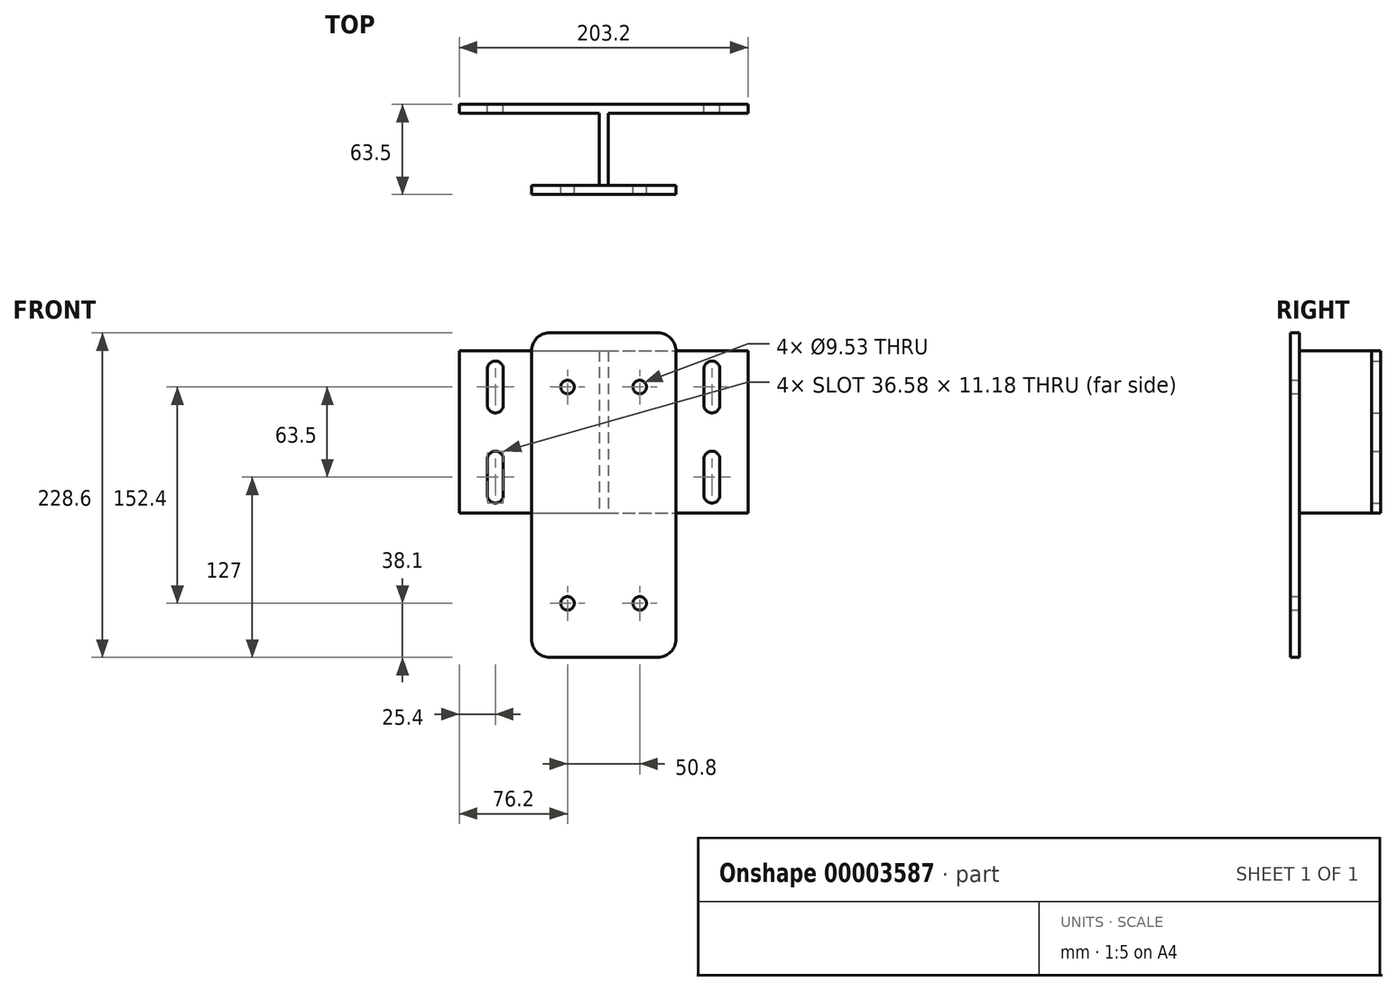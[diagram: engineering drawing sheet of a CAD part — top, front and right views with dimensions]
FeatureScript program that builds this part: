
annotation { "Feature Type Name" : "Feature", "Feature Type Description" : "" }
export const myFeature = defineFeature(function(context is Context, id is Id, definition is map)
    precondition{}
    {
        {
            var Q0;
            Q0=qCreatedBy(makeId("Front.planeOp"),FACE);
            var sketch = newSketch(context, id + "F0", { "sketchPlane" : qUnion([Q0])});
            skLineSegment(sketch, "E0.rect.bottom", {"start": v(-101.6, 57.15) * mm, "end": v(101.6, 57.15) * mm});
            skLineSegment(sketch, "E0.rect.top", {"start": v(-101.6, -57.15) * mm, "end": v(101.6, -57.15) * mm});
            skLineSegment(sketch, "E0.rect.left", {"start": v(-101.6, 57.15) * mm, "end": v(-101.6, -57.15) * mm});
            skLineSegment(sketch, "E0.rect.right", {"start": v(101.6, 57.15) * mm, "end": v(101.6, -57.15) * mm});
            skPoint(sketch, "E0.rect.middle", {"position": v(0, 0) * mm});
            skLineSegment(sketch, "E1", {"start": v(0, 57.15) * mm, "end": v(0, -57.15) * mm, "construction": true});
            skLineSegment(sketch, "E2", {"start": v(-101.6, 0) * mm, "end": v(101.6, 0) * mm, "construction": true});
            skLineSegment(sketch, "E3.0", {"start": v(-76.2, 57.15) * mm, "end": v(-76.2, -57.15) * mm, "construction": true});
            skLineSegment(sketch, "E4.0", {"start": v(-101.6, -31.75) * mm, "end": v(101.6, -31.75) * mm, "construction": true});
            skLineSegment(sketch, "E5.0", {"start": v(-101.6, -44.45) * mm, "end": v(101.6, -44.45) * mm, "construction": true});
            skLineSegment(sketch, "E6.0", {"start": v(-101.6, -19.05) * mm, "end": v(101.6, -19.05) * mm, "construction": true});
            skArc(sketch, "E7", {"start": v(-81.79, -44.45) * mm, "mid": v(-76.2, -50.04) * mm, "end": v(-70.61, -44.45) * mm});
            skArc(sketch, "E8", {"start": v(-70.61, -19.05) * mm, "mid": v(-76.2, -13.46) * mm, "end": v(-81.79, -19.05) * mm});
            skLineSegment(sketch, "E9", {"start": v(-81.79, -19.05) * mm, "end": v(-81.79, -44.45) * mm});
            skLineSegment(sketch, "E10", {"start": v(-70.61, -19.05) * mm, "end": v(-70.61, -44.45) * mm});
            skArc(sketch, "E11.0.MirrorCS", {"start": v(70.61, -19.05) * mm, "mid": v(76.2, -13.46) * mm, "end": v(81.79, -19.05) * mm});
            skLineSegment(sketch, "E12.0.MirrorCS", {"start": v(81.79, -19.05) * mm, "end": v(81.79, -44.45) * mm});
            skLineSegment(sketch, "E13.0.MirrorCS", {"start": v(70.61, -19.05) * mm, "end": v(70.61, -44.45) * mm});
            skArc(sketch, "E14.0.MirrorCS", {"start": v(81.79, -44.45) * mm, "mid": v(76.2, -50.04) * mm, "end": v(70.61, -44.45) * mm});
            skLineSegment(sketch, "E15.0.MirrorCS", {"start": v(70.61, 19.05) * mm, "end": v(70.61, 44.45) * mm});
            skArc(sketch, "E15.1.MirrorCS", {"start": v(81.79, 44.45) * mm, "mid": v(76.2, 50.04) * mm, "end": v(70.61, 44.45) * mm});
            skArc(sketch, "E15.2.MirrorCS", {"start": v(-70.61, 19.05) * mm, "mid": v(-76.2, 13.46) * mm, "end": v(-81.79, 19.05) * mm});
            skArc(sketch, "E15.3.MirrorCS", {"start": v(-81.79, 44.45) * mm, "mid": v(-76.2, 50.04) * mm, "end": v(-70.61, 44.45) * mm});
            skLineSegment(sketch, "E15.4.MirrorCS", {"start": v(-70.61, 19.05) * mm, "end": v(-70.61, 44.45) * mm});
            skArc(sketch, "E15.5.MirrorCS", {"start": v(70.61, 19.05) * mm, "mid": v(76.2, 13.46) * mm, "end": v(81.79, 19.05) * mm});
            skLineSegment(sketch, "E15.6.MirrorCS", {"start": v(81.79, 19.05) * mm, "end": v(81.79, 44.45) * mm});
            skLineSegment(sketch, "E15.7.MirrorCS", {"start": v(-81.79, 19.05) * mm, "end": v(-81.79, 44.45) * mm});
            skSolve(sketch);
        }
        {
            var Q0;
            Q0=makeQuery(id+"F0.imprint","IMPRINT",FACE,{"disambiguationData":[TD([[makeQuery(id+"F0.imprint","IMPRINT",EDGE,{"derivedFrom":sQuery(id+"F0.wireOp",EDGE,"E0.rect.bottom")}),-1.0]])]});
            extrude(context, id + "F1", {"entities" : qUnion([Q0]), "depth" : 6.35 * mm});
        }
        {
            var Q0;
            Q0=makeQuery(id+"F1.opExtrude","CAP_FACE",FACE,{"disambiguationData":[OSD([sQuery(id+"F0.wireOp",EDGE,"E0.rect.bottom"),sQuery(id+"F0.wireOp",EDGE,"E0.rect.top"),sQuery(id+"F0.wireOp",EDGE,"E0.rect.left"),sQuery(id+"F0.wireOp",EDGE,"E0.rect.right"),sQuery(id+"F0.wireOp",EDGE,"E7"),sQuery(id+"F0.wireOp",EDGE,"E8"),sQuery(id+"F0.wireOp",EDGE,"E9"),sQuery(id+"F0.wireOp",EDGE,"E10"),sQuery(id+"F0.wireOp",EDGE,"E11.0.MirrorCS"),sQuery(id+"F0.wireOp",EDGE,"E12.0.MirrorCS"),sQuery(id+"F0.wireOp",EDGE,"E13.0.MirrorCS"),sQuery(id+"F0.wireOp",EDGE,"E14.0.MirrorCS"),sQuery(id+"F0.wireOp",EDGE,"E15.0.MirrorCS"),sQuery(id+"F0.wireOp",EDGE,"E15.1.MirrorCS"),sQuery(id+"F0.wireOp",EDGE,"E15.2.MirrorCS"),sQuery(id+"F0.wireOp",EDGE,"E15.3.MirrorCS"),sQuery(id+"F0.wireOp",EDGE,"E15.4.MirrorCS"),sQuery(id+"F0.wireOp",EDGE,"E15.5.MirrorCS"),sQuery(id+"F0.wireOp",EDGE,"E15.6.MirrorCS"),sQuery(id+"F0.wireOp",EDGE,"E15.7.MirrorCS")])],"isStart":false});
            var sketch = newSketch(context, id + "F2", { "sketchPlane" : qUnion([Q0])});
            skLineSegment(sketch, "E16", {"start": v(0, 57.15) * mm, "end": v(0, -57.15) * mm, "construction": true});
            skLineSegment(sketch, "E17.0", {"start": v(-3.17, 57.15) * mm, "end": v(-3.18, -57.15) * mm});
            skLineSegment(sketch, "E18.0", {"start": v(3.18, 57.15) * mm, "end": v(3.17, -57.15) * mm});
            skLineSegment(sketch, "E19", {"start": v(-3.17, 57.15) * mm, "end": v(3.18, 57.15) * mm});
            skLineSegment(sketch, "E20", {"start": v(3.17, -57.15) * mm, "end": v(-3.18, -57.15) * mm});
            skSolve(sketch);
        }
        {
            var Q0;
            Q0 = qSketchRegion(id + "F2", true);
            extrude(context, id + "F3", {"entities" : qUnion([Q0]), "operationType" : NewBodyOperationType.ADD, "depth" : 50.8 * mm});
        }
        {
            var Q0;
            Q0=makeQuery(id+"F3.opExtrude","CAP_FACE",FACE,{"disambiguationData":[OSD([sQuery(id+"F2.wireOp",EDGE,"E17.0"),sQuery(id+"F2.wireOp",EDGE,"E18.0"),sQuery(id+"F2.wireOp",EDGE,"E19"),sQuery(id+"F2.wireOp",EDGE,"E20")])],"isStart":false});
            var sketch = newSketch(context, id + "F4", { "sketchPlane" : qUnion([Q0])});
            skLineSegment(sketch, "E21", {"start": v(0, 57.15) * mm, "end": v(0, -57.15) * mm, "construction": true});
            skLineSegment(sketch, "E22.0", {"start": v(-3.18, -57.15) * mm, "end": v(3.17, -57.15) * mm});
            skLineSegment(sketch, "E23.0", {"start": v(-38.1, -158.75) * mm, "end": v(38.1, -158.75) * mm});
            skLineSegment(sketch, "E24.0", {"start": v(-50.8, 57.15) * mm, "end": v(-50.8, -146.05) * mm});
            skLineSegment(sketch, "E25.0", {"start": v(50.8, 57.15) * mm, "end": v(50.8, -146.05) * mm});
            skLineSegment(sketch, "E26.0", {"start": v(-38.1, 69.85) * mm, "end": v(38.1, 69.85) * mm});
            skPoint(sketch, "E27.visualSharp", {"position": v(-50.8, -158.75) * mm});
            skArc(sketch, "E27.filletArc", {"start": v(-50.8, -146.05) * mm, "mid": v(-47.08, -155.03) * mm, "end": v(-38.1, -158.75) * mm});
            skPoint(sketch, "E28.visualSharp", {"position": v(50.8, -158.75) * mm});
            skArc(sketch, "E28.filletArc", {"start": v(38.1, -158.75) * mm, "mid": v(47.08, -155.03) * mm, "end": v(50.8, -146.05) * mm});
            skPoint(sketch, "E29.visualSharp", {"position": v(50.8, 69.85) * mm});
            skArc(sketch, "E29.filletArc", {"start": v(50.8, 57.15) * mm, "mid": v(47.08, 66.13) * mm, "end": v(38.1, 69.85) * mm});
            skPoint(sketch, "E30.visualSharp", {"position": v(-50.8, 69.85) * mm});
            skArc(sketch, "E30.filletArc", {"start": v(-38.1, 69.85) * mm, "mid": v(-47.08, 66.13) * mm, "end": v(-50.8, 57.15) * mm});
            skLineSegment(sketch, "E31.0", {"start": v(-25.4, -120.65) * mm, "end": v(25.4, -120.65) * mm, "construction": true});
            skLineSegment(sketch, "E32.0", {"start": v(-25.4, 31.75) * mm, "end": v(25.4, 31.75) * mm, "construction": true});
            skLineSegment(sketch, "E33.0", {"start": v(-25.4, 31.75) * mm, "end": v(-25.4, -120.65) * mm, "construction": true});
            skLineSegment(sketch, "E34.0", {"start": v(50.1, 57.15) * mm, "end": v(50.1, -57.15) * mm, "construction": true});
            skLineSegment(sketch, "E35.0", {"start": v(25.4, 31.75) * mm, "end": v(25.4, -120.65) * mm, "construction": true});
            skCircle(sketch, "E36", {"center": v(-25.4, 31.75) * mm, "radius": 4.76 * mm});
            skCircle(sketch, "E37", {"center": v(25.4, 31.75) * mm, "radius": 4.76 * mm});
            skCircle(sketch, "E38", {"center": v(25.4, -120.65) * mm, "radius": 4.76 * mm});
            skCircle(sketch, "E39", {"center": v(-25.4, -120.65) * mm, "radius": 4.76 * mm});
            skSolve(sketch);
        }
        {
            var Q0;
            Q0=makeQuery(id+"F4.imprint","IMPRINT",FACE,{"disambiguationData":[TD([[makeQuery(id+"F4.imprint","IMPRINT",EDGE,{"derivedFrom":sQuery(id+"F4.wireOp",EDGE,"E22.0")}),-1.0]])]});
            var Q1;
            Q1=makeQuery(id+"F4.imprint","IMPRINT",FACE,{"disambiguationData":[TD([[makeQuery(id+"F4.imprint","IMPRINT",EDGE,{"derivedFrom":sQuery(id+"F4.wireOp",EDGE,"E22.0")}),1.0]])]});
            extrude(context, id + "F5", {"entities" : qUnion([Q0, Q1]), "operationType" : NewBodyOperationType.ADD, "depth" : 6.35 * mm});
        }
    });
